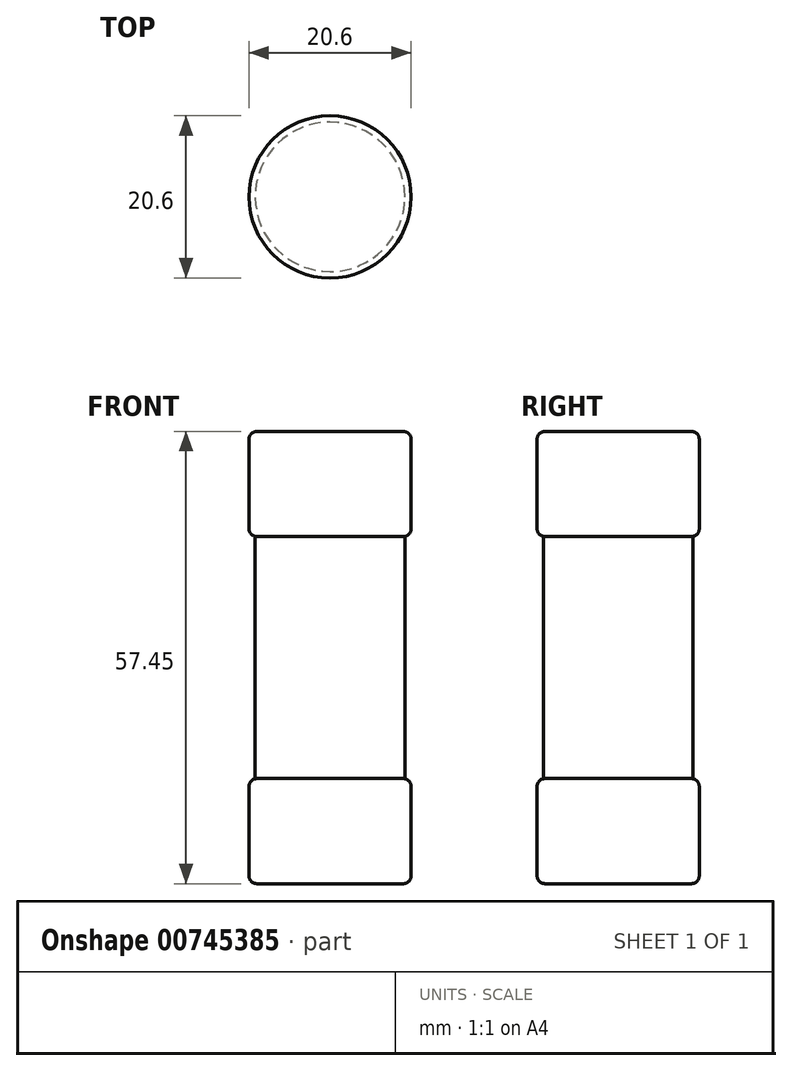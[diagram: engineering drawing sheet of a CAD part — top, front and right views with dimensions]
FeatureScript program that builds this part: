
annotation { "Feature Type Name" : "Feature", "Feature Type Description" : "" }
export const myFeature = defineFeature(function(context is Context, id is Id, definition is map)
    precondition{}
    {
        {
            var Q0;
            Q0=qCreatedBy(makeId("Top.planeOp"),FACE);
            var sketch = newSketch(context, id + "F0", { "sketchPlane" : qUnion([Q0])});
            skCircle(sketch, "E0", {"center": v(0, 0) * mm, "radius": 10.3 * mm});
            skSolve(sketch);
        }
        {
            var Q0;
            Q0=qSketchRegion(id+"F0",true);
            extrude(context, id + "F1", {"entities" : qUnion([Q0]), "depth" : 13.35 * mm, "offsetDistance" : 25 * mm});
        }
        {
            var Q0;
            Q0=makeQuery(id+"F1.opExtrude","CAP_FACE",FACE,{"disambiguationData":[OSD([sQuery(id+"F0.wireOp",EDGE,"E0")])],"isStart":false});
            var sketch = newSketch(context, id + "F2", { "sketchPlane" : qUnion([Q0])});
            skCircle(sketch, "E1", {"center": v(0, 0) * mm, "radius": 9.5 * mm});
            skSolve(sketch);
        }
        {
            var Q0;
            Q0=qSketchRegion(id+"F2",true);
            extrude(context, id + "F3", {"entities" : qUnion([Q0]), "depth" : 30.75 * mm, "offsetDistance" : 25 * mm});
        }
        {
            var Q0;
            Q0=makeQuery(id+"F3.opExtrude","CAP_FACE",FACE,{"disambiguationData":[OSD([sQuery(id+"F2.wireOp",EDGE,"E1")])],"isStart":false});
            var sketch = newSketch(context, id + "F4", { "sketchPlane" : qUnion([Q0])});
            skCircle(sketch, "E2", {"center": v(0, 0) * mm, "radius": 10.3 * mm});
            skSolve(sketch);
        }
        {
            var Q0;
            Q0=qSketchRegion(id+"F4",true);
            extrude(context, id + "F5", {"entities" : qUnion([Q0]), "depth" : 13.35 * mm, "offsetDistance" : 25 * mm});
        }
        {
            var Q0;
            Q0=makeQuery(id+"F5.opExtrude","CAP_EDGE",EDGE,{"disambiguationData":[OSD([sQuery(id+"F4.wireOp",EDGE,"E2")])],"isStart":false});
            var Q1;
            Q1=makeQuery(id+"F1.opExtrude","CAP_EDGE",EDGE,{"disambiguationData":[OSD([sQuery(id+"F0.wireOp",EDGE,"E0")])],"isStart":true});
            var Q2;
            Q2=makeQuery(id+"F5.opExtrude","CAP_EDGE",EDGE,{"disambiguationData":[OSD([sQuery(id+"F4.wireOp",EDGE,"E2")])],"isStart":true});
            var Q3;
            Q3=makeQuery(id+"F1.opExtrude","CAP_EDGE",EDGE,{"disambiguationData":[OSD([sQuery(id+"F0.wireOp",EDGE,"E0")])],"isStart":false});
            fillet(context, id + "F6", {"entities" : qUnion([Q0, Q1, Q2, Q3]), "radius" : 1 * mm, "tangentPropagation" : true, "defaultsChanged" : true, "vertexSettings" : [], "allowEdgeOverflow" : false});
        }
    });
